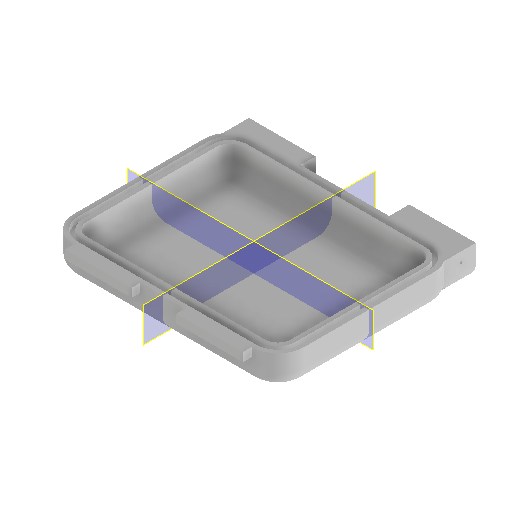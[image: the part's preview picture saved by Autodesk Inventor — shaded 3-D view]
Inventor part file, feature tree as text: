
AUTODESK INVENTOR PART (.ipt)
format: ipt  version: 2024.1 (Build 281209000, 209)  size: 2,345,472 bytes
history: native  units: mm
features: extrude x5, sketch x5, other x3, projected_geometry x3, plane x2, fillet x1, reference x1
ambient origin geometry x8: Origin, YZ Plane, XZ Plane, XY Plane, X Axis, Y Axis, Z Axis, Center Point
bodies: Volumenkörper1 (feature_tree)
feature tree (20):
  extrude  "Extrusion1"  Depth=233.0mm
  extrude  "Extrusion2"  Depth=15.0mm
  fillet  "Rundung1"  Radius=30.0mm
  extrude  "Extrusion3"  Depth=15.0mm
  extrude  "Extrusion4"  Depth=5.0mm
  plane  "Arbeitsebene1"
  plane  "Arbeitsebene2"
  extrude  "Extrusion5"  Depth=5.0mm
  sketch  "Skizze1"  dims[d10=233.0mm d11=178.0mm]
  other  "Bild1"
  sketch  "Skizze2"  dims[d13=15.0mm d14=15.0mm d15=30.0mm d16=0.0mm]
  projected_geometry  "Projizierte Kontur1"
  sketch  "Skizze3"  dims[d17=6.0mm d18=0.0mm d19=15.0mm]
  projected_geometry  "Projizierte Kontur2"
  sketch  "Skizze4"  dims[d20=5.0mm d21=5.0mm]
  projected_geometry  "Projizierte Kontur3"
  sketch  "Skizze5"  dims[d22=6.0mm d23=0.0mm d24=5.0mm d25=17.0mm d26=76.0mm d27=5.0mm d28=76.0mm d30=76.0mm d31=10.0mm d32=76.0mm d33=10.0mm d34=0.0mm d35=0.0mm d36=0.0mm]
  reference  "Referenz1"
  other  "Assembly_Planktoscope_Uc2version_wormdrive_V3.iam"
  other  "00_OutdoorCase_Type2000_base:1"
